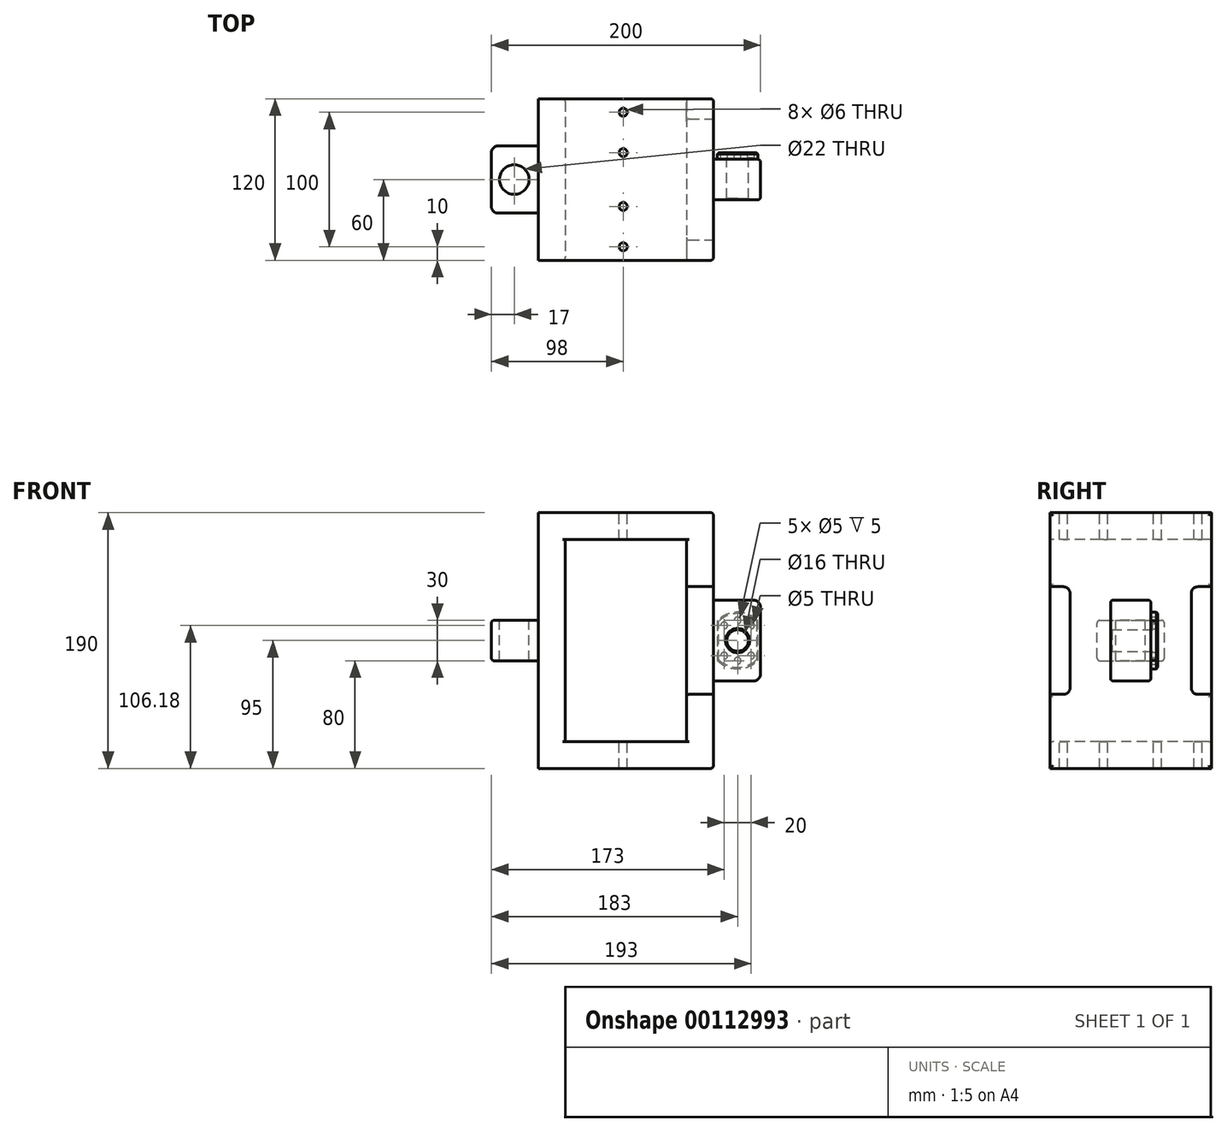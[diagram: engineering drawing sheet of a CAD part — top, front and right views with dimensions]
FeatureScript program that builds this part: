
annotation { "Feature Type Name" : "Feature", "Feature Type Description" : "" }
export const myFeature = defineFeature(function(context is Context, id is Id, definition is map)
    precondition{}
    {
        {
            var Q0;
            Q0=qCreatedBy(makeId("Front.planeOp"),FACE);
            var sketch = newSketch(context, id + "F0", { "sketchPlane" : qUnion([Q0])});
            skLineSegment(sketch, "E0.bottom", {"start": v(-45, 75) * mm, "end": v(45, 75) * mm});
            skLineSegment(sketch, "E0.top", {"start": v(-45, -75) * mm, "end": v(45, -75) * mm});
            skLineSegment(sketch, "E0.left", {"start": v(-45, 75) * mm, "end": v(-45, -75) * mm});
            skPoint(sketch, "E0.middle", {"position": v(0, 0) * mm});
            skLineSegment(sketch, "E1.bottom", {"start": v(-65, 95) * mm, "end": v(45, 95) * mm});
            skLineSegment(sketch, "E1.top", {"start": v(-65, -95) * mm, "end": v(45, -95) * mm});
            skLineSegment(sketch, "E1.left", {"start": v(-65, 95) * mm, "end": v(-65, -95) * mm});
            skLineSegment(sketch, "E2.bottom", {"start": v(45, 95) * mm, "end": v(65, 95) * mm});
            skLineSegment(sketch, "E2.top", {"start": v(45, -95) * mm, "end": v(65, -95) * mm});
            skLineSegment(sketch, "E2.left", {"start": v(45, 75) * mm, "end": v(45, -75) * mm});
            skLineSegment(sketch, "E2.right", {"start": v(65, 95) * mm, "end": v(65, -95) * mm});
            skSolve(sketch);
        }
        {
            var Q0;
            Q0=makeQuery(id+"F0.imprint","IMPRINT",FACE,{"disambiguationData":[TD([[makeQuery(id+"F0.imprint","IMPRINT",EDGE,{"derivedFrom":sQuery(id+"F0.wireOp",EDGE,"E0.bottom")}),1.0]])]});
            extrude(context, id + "F1", {"entities" : qUnion([Q0]), "oppositeDirection" : true, "depth" : 120 * mm});
        }
        {
            var Q0;
            Q0=makeQuery(id+"F1.opExtrude","SWEPT_FACE",FACE,{"disambiguationData":[OSD([sQuery(id+"F0.wireOp",EDGE,"E1.bottom")])]});
            var sketch = newSketch(context, id + "F2", { "sketchPlane" : qUnion([Q0])});
            skCircle(sketch, "E3", {"center": v(-2, 110) * mm, "radius": 3 * mm});
            skCircle(sketch, "E4", {"center": v(-2, 10) * mm, "radius": 3 * mm});
            skCircle(sketch, "E5", {"center": v(-2, 80) * mm, "radius": 3 * mm});
            skCircle(sketch, "E6", {"center": v(-2, 40) * mm, "radius": 3 * mm});
            skSolve(sketch);
        }
        {
            var Q0;
            Q0=makeQuery(id+"F2.imprint","IMPRINT",FACE,{"disambiguationData":[TD([[makeQuery(id+"F2.imprint","IMPRINT",EDGE,{"derivedFrom":sQuery(id+"F2.wireOp",EDGE,"E3")}),1.0]])]});
            var Q1;
            Q1=makeQuery(id+"F2.imprint","IMPRINT",FACE,{"disambiguationData":[TD([[makeQuery(id+"F2.imprint","IMPRINT",EDGE,{"derivedFrom":sQuery(id+"F2.wireOp",EDGE,"E5")}),1.0]])]});
            var Q2;
            Q2=makeQuery(id+"F2.imprint","IMPRINT",FACE,{"disambiguationData":[TD([[makeQuery(id+"F2.imprint","IMPRINT",EDGE,{"derivedFrom":sQuery(id+"F2.wireOp",EDGE,"E6")}),1.0]])]});
            var Q3;
            Q3=makeQuery(id+"F2.imprint","IMPRINT",FACE,{"disambiguationData":[TD([[makeQuery(id+"F2.imprint","IMPRINT",EDGE,{"derivedFrom":sQuery(id+"F2.wireOp",EDGE,"E4")}),1.0]])]});
            extrude(context, id + "F3", {"entities" : qUnion([Q0, Q1, Q2, Q3]), "operationType" : NewBodyOperationType.REMOVE, "oppositeDirection" : true, "depth" : 200 * mm});
        }
        {
            var Q0;
            Q0=makeQuery(id+"F1.opExtrude","SWEPT_FACE",FACE,{"disambiguationData":[OSD([sQuery(id+"F0.wireOp",EDGE,"E2.right")])]});
            var sketch = newSketch(context, id + "F4", { "sketchPlane" : qUnion([Q0])});
            skLineSegment(sketch, "E7.bottom", {"start": v(45, -30) * mm, "end": v(75, -30) * mm});
            skLineSegment(sketch, "E7.top", {"start": v(45, 30) * mm, "end": v(75, 30) * mm});
            skLineSegment(sketch, "E7.left", {"start": v(45, -30) * mm, "end": v(45, 30) * mm});
            skLineSegment(sketch, "E7.right", {"start": v(75, -30) * mm, "end": v(75, 30) * mm});
            skPoint(sketch, "E7.middle", {"position": v(60, 0) * mm});
            skSolve(sketch);
        }
        {
            var Q0;
            Q0=makeQuery(id+"F4.imprint","IMPRINT",FACE,{"disambiguationData":[TD([[makeQuery(id+"F4.imprint","IMPRINT",EDGE,{"derivedFrom":sQuery(id+"F4.wireOp",EDGE,"E7.bottom")}),1.0]])]});
            extrude(context, id + "F5", {"entities" : qUnion([Q0]), "operationType" : NewBodyOperationType.ADD, "depth" : 35 * mm});
        }
        {
            var Q0;
            Q0=makeQuery(id+"F5.opExtrude","SWEPT_FACE",FACE,{"disambiguationData":[OSD([sQuery(id+"F4.wireOp",EDGE,"E7.right")])]});
            var sketch = newSketch(context, id + "F6", { "sketchPlane" : qUnion([Q0])});
            skCircle(sketch, "E8", {"center": v(-83, 0) * mm, "radius": 12.5 * mm});
            skSolve(sketch);
        }
        {
            var Q0;
            Q0=makeQuery(id+"F6.imprint","IMPRINT",FACE,{"disambiguationData":[TD([[makeQuery(id+"F6.imprint","IMPRINT",EDGE,{"derivedFrom":sQuery(id+"F6.wireOp",EDGE,"E8")}),1.0]])]});
            extrude(context, id + "F7", {"entities" : qUnion([Q0]), "operationType" : NewBodyOperationType.REMOVE, "oppositeDirection" : true, "depth" : 30 * mm});
        }
        {
            var Q0;
            Q0=makeQuery(id+"F5.opExtrude","SWEPT_FACE",FACE,{"disambiguationData":[OSD([sQuery(id+"F4.wireOp",EDGE,"E7.right")])]});
            var sketch = newSketch(context, id + "F8", { "sketchPlane" : qUnion([Q0])});
            skCircle(sketch, "E9", {"center": v(-83, 0) * mm, "radius": 8 * mm});
            skCircle(sketch, "E10", {"center": v(-83, 0) * mm, "radius": 12.5 * mm});
            skSolve(sketch);
        }
        {
            var Q0;
            Q0=makeQuery(id+"F8.imprint","IMPRINT",FACE,{"disambiguationData":[TD([[makeQuery(id+"F8.imprint","IMPRINT",EDGE,{"derivedFrom":sQuery(id+"F8.wireOp",EDGE,"E9")}),-1.0]])]});
            var Q1;
            Q1=sQuery(id+"F8.wireOp",EDGE,"E9");
            var Q2;
            Q2=sQuery(id+"F8.wireOp",EDGE,"E10");
            extrude(context, id + "F9", {"entities" : qUnion([Q0]), "surfaceEntities" : qUnion([Q1, Q2]), "oppositeDirection" : true, "depth" : 30 * mm});
        }
        {
            var Q0;
            Q0=makeQuery(id+"F9.opExtrude","CAP_FACE",FACE,{"disambiguationData":[OSD([sQuery(id+"F8.wireOp",EDGE,"E9"),sQuery(id+"F8.wireOp",EDGE,"E10")])],"isStart":true});
            var sketch = newSketch(context, id + "F10", { "sketchPlane" : qUnion([Q0])});
            skArc(sketch, "E11", {"start": v(-98, -14.7) * mm, "mid": v(-83, -21) * mm, "end": v(-68, -14.7) * mm});
            skLineSegment(sketch, "E12", {"start": v(-98, 14.7) * mm, "end": v(-98, -14.7) * mm});
            skLineSegment(sketch, "E13", {"start": v(-68, 14.7) * mm, "end": v(-68, -14.7) * mm});
            skArc(sketch, "E14.trimOffspring", {"start": v(-68, 14.7) * mm, "mid": v(-83, 21) * mm, "end": v(-98, 14.7) * mm});
            skSolve(sketch);
        }
        {
            var Q0;
            Q0=makeQuery(id+"F10.imprint","IMPRINT",FACE,{"disambiguationData":[TD([[makeQuery(id+"F10.imprint","IMPRINT",EDGE,{"derivedFrom":makeQuery(id+"F9.opExtrude","CAP_EDGE",EDGE,{"disambiguationData":[OSD([sQuery(id+"F8.wireOp",EDGE,"E9")])],"isStart":true})}),1.0]])]});
            var Q1;
            Q1=makeQuery(id+"F10.imprint","IMPRINT",FACE,{"disambiguationData":[TD([[makeQuery(id+"F10.imprint","IMPRINT",EDGE,{"derivedFrom":makeQuery(id+"F9.opExtrude","CAP_EDGE",EDGE,{"disambiguationData":[OSD([sQuery(id+"F8.wireOp",EDGE,"E9")])],"isStart":true})}),-1.0]])]});
            var Q2;
            Q2=makeQuery(id+"F10.imprint","IMPRINT",FACE,{"disambiguationData":[TD([[makeQuery(id+"F10.imprint","IMPRINT",EDGE,{"derivedFrom":sQuery(id+"F10.wireOp",EDGE,"E11")}),1.0]])]});
            extrude(context, id + "F11", {"entities" : qUnion([Q0, Q1, Q2]), "operationType" : NewBodyOperationType.ADD, "depth" : 5 * mm});
        }
        {
            var Q0;
            Q0=makeQuery(id+"F11.opExtrude","CAP_FACE",FACE,{"disambiguationData":[OSD([sQuery(id+"F10.wireOp",EDGE,"E11")])],"isStart":false});
            var sketch = newSketch(context, id + "F12", { "sketchPlane" : qUnion([Q0])});
            skCircle(sketch, "E15", {"center": v(-83, 0) * mm, "radius": 8 * mm});
            skSolve(sketch);
        }
        {
            var Q0;
            Q0=makeQuery(id+"F12.imprint","IMPRINT",FACE,{"disambiguationData":[TD([[makeQuery(id+"F12.imprint","IMPRINT",EDGE,{"derivedFrom":sQuery(id+"F12.wireOp",EDGE,"E15")}),1.0]])]});
            extrude(context, id + "F13", {"entities" : qUnion([Q0]), "operationType" : NewBodyOperationType.REMOVE, "oppositeDirection" : true, "depth" : 25 * mm});
        }
        {
            var Q0;
            Q0=makeQuery(id+"F11.opExtrude","CAP_EDGE",EDGE,{"disambiguationData":[OSD([sQuery(id+"F10.wireOp",EDGE,"E11")])],"isStart":false});
            var Q1;
            Q1=makeQuery(id+"F13.boolean.opBoolean","COPY",EDGE,{"derivedFrom":makeQuery(id+"F13.opExtrude","CAP_EDGE",EDGE,{"disambiguationData":[OSD([sQuery(id+"F12.wireOp",EDGE,"E15")])],"isStart":true})});
            var Q2;
            Q2=makeQuery(id+"F9.opExtrude","CAP_EDGE",EDGE,{"disambiguationData":[OSD([sQuery(id+"F8.wireOp",EDGE,"E9")])],"isStart":false});
            var Q3;
            Q3=makeQuery(id+"F11.opExtrude","CAP_EDGE",EDGE,{"disambiguationData":[OSD([sQuery(id+"F10.wireOp",EDGE,"E14.trimOffspring")])],"isStart":false});
            var Q4;
            Q4=makeQuery(id+"F11.opExtrude","CAP_EDGE",EDGE,{"disambiguationData":[OSD([sQuery(id+"F10.wireOp",EDGE,"E12")])],"isStart":false});
            var Q5;
            Q5=makeQuery(id+"F11.opExtrude","CAP_EDGE",EDGE,{"disambiguationData":[OSD([sQuery(id+"F10.wireOp",EDGE,"E13")])],"isStart":false});
            chamfer(context, id + "F14", {"entities" : qUnion([Q0, Q1, Q2, Q3, Q4, Q5]), "width" : 1 * mm, "tangentPropagation" : true});
        }
        {
            var Q0;
            Q0=makeQuery(id+"F1.opExtrude","SWEPT_FACE",FACE,{"disambiguationData":[OSD([sQuery(id+"F0.wireOp",EDGE,"E2.right")])]});
            var sketch = newSketch(context, id + "F15", { "sketchPlane" : qUnion([Q0])});
            skLineSegment(sketch, "E16.bottom", {"start": v(0, -40) * mm, "end": v(10, -40) * mm});
            skLineSegment(sketch, "E16.top", {"start": v(0, 40) * mm, "end": v(10, 40) * mm});
            skLineSegment(sketch, "E16.left", {"start": v(0, -40) * mm, "end": v(0, 40) * mm});
            skLineSegment(sketch, "E16.right", {"start": v(15, -35) * mm, "end": v(15, 35) * mm});
            skPoint(sketch, "E16.middle", {"position": v(7.5, 0) * mm});
            skLineSegment(sketch, "E17.bottom", {"start": v(120, -40) * mm, "end": v(110, -40) * mm});
            skLineSegment(sketch, "E17.top", {"start": v(120, 40) * mm, "end": v(110, 40) * mm});
            skLineSegment(sketch, "E17.left", {"start": v(120, -40) * mm, "end": v(120, 40) * mm});
            skLineSegment(sketch, "E17.right", {"start": v(105, -35) * mm, "end": v(105, 35) * mm});
            skPoint(sketch, "E17.middle", {"position": v(112.5, 0) * mm});
            skPoint(sketch, "E18.visualSharp", {"position": v(105, 40) * mm});
            skArc(sketch, "E18.filletArc", {"start": v(110, 40) * mm, "mid": v(106.46, 38.54) * mm, "end": v(105, 35) * mm});
            skPoint(sketch, "E19.visualSharp", {"position": v(105, -40) * mm});
            skArc(sketch, "E19.filletArc", {"start": v(105, -35) * mm, "mid": v(106.46, -38.54) * mm, "end": v(110, -40) * mm});
            skPoint(sketch, "E20.visualSharp", {"position": v(15, -40) * mm});
            skArc(sketch, "E20.filletArc", {"start": v(10, -40) * mm, "mid": v(13.54, -38.54) * mm, "end": v(15, -35) * mm});
            skPoint(sketch, "E21.visualSharp", {"position": v(15, 40) * mm});
            skArc(sketch, "E21.filletArc", {"start": v(15, 35) * mm, "mid": v(13.54, 38.54) * mm, "end": v(10, 40) * mm});
            skSolve(sketch);
        }
        {
            var Q0;
            Q0=makeQuery(id+"F15.imprint","IMPRINT",FACE,{"disambiguationData":[TD([[makeQuery(id+"F15.imprint","IMPRINT",EDGE,{"derivedFrom":sQuery(id+"F15.wireOp",EDGE,"E16.bottom")}),1.0]])]});
            var Q1;
            Q1=makeQuery(id+"F15.imprint","IMPRINT",FACE,{"disambiguationData":[TD([[makeQuery(id+"F15.imprint","IMPRINT",EDGE,{"derivedFrom":sQuery(id+"F15.wireOp",EDGE,"E17.bottom")}),-1.0]])]});
            extrude(context, id + "F16", {"entities" : qUnion([Q0, Q1]), "operationType" : NewBodyOperationType.REMOVE, "oppositeDirection" : true, "depth" : 25 * mm});
        }
        {
            var Q0;
            Q0=makeQuery(id+"F1.opExtrude","SWEPT_FACE",FACE,{"disambiguationData":[OSD([sQuery(id+"F0.wireOp",EDGE,"E1.left")])]});
            var sketch = newSketch(context, id + "F17", { "sketchPlane" : qUnion([Q0])});
            skLineSegment(sketch, "E22.bottom", {"start": v(-35, -15) * mm, "end": v(-85, -15) * mm});
            skLineSegment(sketch, "E22.top", {"start": v(-35, 15) * mm, "end": v(-85, 15) * mm});
            skLineSegment(sketch, "E22.left", {"start": v(-35, -15) * mm, "end": v(-35, 15) * mm});
            skLineSegment(sketch, "E22.right", {"start": v(-85, -15) * mm, "end": v(-85, 15) * mm});
            skPoint(sketch, "E22.middle", {"position": v(-60, 0) * mm});
            skSolve(sketch);
        }
        {
            var Q0;
            Q0=makeQuery(id+"F17.imprint","IMPRINT",FACE,{"disambiguationData":[TD([[makeQuery(id+"F17.imprint","IMPRINT",EDGE,{"derivedFrom":sQuery(id+"F17.wireOp",EDGE,"E22.bottom")}),-1.0]])]});
            extrude(context, id + "F18", {"entities" : qUnion([Q0]), "operationType" : NewBodyOperationType.ADD, "depth" : 35 * mm});
        }
        {
            var Q0;
            Q0=makeQuery(id+"F18.opExtrude","SWEPT_FACE",FACE,{"disambiguationData":[OSD([sQuery(id+"F17.wireOp",EDGE,"E22.top")])]});
            var sketch = newSketch(context, id + "F19", { "sketchPlane" : qUnion([Q0])});
            skCircle(sketch, "E23", {"center": v(-83, 60) * mm, "radius": 11 * mm});
            skSolve(sketch);
        }
        {
            var Q0;
            Q0=makeQuery(id+"F19.imprint","IMPRINT",FACE,{"disambiguationData":[TD([[makeQuery(id+"F19.imprint","IMPRINT",EDGE,{"derivedFrom":sQuery(id+"F19.wireOp",EDGE,"E23")}),1.0]])]});
            extrude(context, id + "F20", {"entities" : qUnion([Q0]), "operationType" : NewBodyOperationType.REMOVE, "oppositeDirection" : true, "depth" : 30 * mm});
        }
        {
            var Q0;
            Q0=makeQuery(id+"F18.opExtrude","CAP_EDGE",EDGE,{"disambiguationData":[OSD([sQuery(id+"F17.wireOp",EDGE,"E22.left")])],"isStart":false});
            var Q1;
            Q1=makeQuery(id+"F18.opExtrude","CAP_EDGE",EDGE,{"disambiguationData":[OSD([sQuery(id+"F17.wireOp",EDGE,"E22.right")])],"isStart":false});
            fillet(context, id + "F21", {"entities" : qUnion([Q0, Q1]), "radius" : 5 * mm, "tangentPropagation" : true, "allowEdgeOverflow" : false});
        }
        {
            var Q0;
            Q0=makeQuery(id+"F11.opExtrude","CAP_FACE",FACE,{"disambiguationData":[OSD([sQuery(id+"F10.wireOp",EDGE,"E11"),sQuery(id+"F10.wireOp",EDGE,"E12"),sQuery(id+"F10.wireOp",EDGE,"E13"),sQuery(id+"F10.wireOp",EDGE,"E14.trimOffspring")])],"isStart":false});
            var sketch = newSketch(context, id + "F22", { "sketchPlane" : qUnion([Q0])});
            skCircle(sketch, "E24", {"center": v(-83, 0) * mm, "radius": 15 * mm, "construction": true});
            skCircle(sketch, "E25", {"center": v(-83, 15) * mm, "radius": 2.5 * mm});
            skCircle(sketch, "E26", {"center": v(-83, -15) * mm, "radius": 2.5 * mm});
            skCircle(sketch, "E27", {"center": v(-93, 11.18) * mm, "radius": 2.5 * mm});
            skCircle(sketch, "E28", {"center": v(-73, 11.18) * mm, "radius": 2.5 * mm});
            skCircle(sketch, "E29", {"center": v(-93, -11.18) * mm, "radius": 2.5 * mm});
            skCircle(sketch, "E30", {"center": v(-73, -11.18) * mm, "radius": 2.5 * mm});
            skSolve(sketch);
        }
        {
            var Q0;
            Q0=makeQuery(id+"F22.imprint","IMPRINT",FACE,{"disambiguationData":[TD([[makeQuery(id+"F22.imprint","IMPRINT",EDGE,{"derivedFrom":sQuery(id+"F22.wireOp",EDGE,"E27")}),1.0]])]});
            var Q1;
            Q1=makeQuery(id+"F22.imprint","IMPRINT",FACE,{"disambiguationData":[TD([[makeQuery(id+"F22.imprint","IMPRINT",EDGE,{"derivedFrom":sQuery(id+"F22.wireOp",EDGE,"E25")}),1.0]])]});
            var Q2;
            Q2=makeQuery(id+"F22.imprint","IMPRINT",FACE,{"disambiguationData":[TD([[makeQuery(id+"F22.imprint","IMPRINT",EDGE,{"derivedFrom":sQuery(id+"F22.wireOp",EDGE,"E28")}),1.0]])]});
            var Q3;
            Q3=makeQuery(id+"F22.imprint","IMPRINT",FACE,{"disambiguationData":[TD([[makeQuery(id+"F22.imprint","IMPRINT",EDGE,{"derivedFrom":sQuery(id+"F22.wireOp",EDGE,"E30")}),1.0]])]});
            var Q4;
            Q4=makeQuery(id+"F22.imprint","IMPRINT",FACE,{"disambiguationData":[TD([[makeQuery(id+"F22.imprint","IMPRINT",EDGE,{"derivedFrom":sQuery(id+"F22.wireOp",EDGE,"E26")}),1.0]])]});
            var Q5;
            Q5=makeQuery(id+"F22.imprint","IMPRINT",FACE,{"disambiguationData":[TD([[makeQuery(id+"F22.imprint","IMPRINT",EDGE,{"derivedFrom":sQuery(id+"F22.wireOp",EDGE,"E29")}),1.0]])]});
            extrude(context, id + "F23", {"entities" : qUnion([Q0, Q1, Q2, Q3, Q4, Q5]), "operationType" : NewBodyOperationType.REMOVE, "oppositeDirection" : true, "depth" : 5 * mm});
        }
        {
            var Q0;
            Q0=makeQuery(id+"F23.boolean.opBoolean","COPY",EDGE,{"derivedFrom":makeQuery(id+"F23.opExtrude","CAP_EDGE",EDGE,{"disambiguationData":[OSD([sQuery(id+"F22.wireOp",EDGE,"E27")])],"isStart":false})});
            var Q1;
            Q1=makeQuery(id+"F23.boolean.opBoolean","COPY",EDGE,{"derivedFrom":makeQuery(id+"F23.opExtrude","CAP_EDGE",EDGE,{"disambiguationData":[OSD([sQuery(id+"F22.wireOp",EDGE,"E25")])],"isStart":true})});
            var Q2;
            Q2=makeQuery(id+"F23.boolean.opBoolean","COPY",EDGE,{"derivedFrom":makeQuery(id+"F23.opExtrude","CAP_EDGE",EDGE,{"disambiguationData":[OSD([sQuery(id+"F22.wireOp",EDGE,"E28")])],"isStart":true})});
            var Q3;
            Q3=makeQuery(id+"F23.boolean.opBoolean","COPY",EDGE,{"derivedFrom":makeQuery(id+"F23.opExtrude","CAP_EDGE",EDGE,{"disambiguationData":[OSD([sQuery(id+"F22.wireOp",EDGE,"E30")])],"isStart":true})});
            var Q4;
            Q4=makeQuery(id+"F23.boolean.opBoolean","COPY",EDGE,{"derivedFrom":makeQuery(id+"F23.opExtrude","CAP_EDGE",EDGE,{"disambiguationData":[OSD([sQuery(id+"F22.wireOp",EDGE,"E26")])],"isStart":true})});
            var Q5;
            Q5=makeQuery(id+"F23.boolean.opBoolean","COPY",EDGE,{"derivedFrom":makeQuery(id+"F23.opExtrude","CAP_EDGE",EDGE,{"disambiguationData":[OSD([sQuery(id+"F22.wireOp",EDGE,"E29")])],"isStart":true})});
            var Q6;
            Q6=makeQuery(id+"F23.boolean.opBoolean","COPY",EDGE,{"derivedFrom":makeQuery(id+"F23.opExtrude","CAP_EDGE",EDGE,{"disambiguationData":[OSD([sQuery(id+"F22.wireOp",EDGE,"E27")])],"isStart":true})});
            chamfer(context, id + "F24", {"entities" : qUnion([Q0, Q1, Q2, Q3, Q4, Q5, Q6]), "width" : 1 * mm, "tangentPropagation" : true});
        }
        {
            var Q0;
            Q0=makeQuery(id+"F5.opExtrude","CAP_EDGE",EDGE,{"disambiguationData":[OSD([sQuery(id+"F4.wireOp",EDGE,"E7.top")])],"isStart":false});
            var Q1;
            Q1=makeQuery(id+"F5.opExtrude","CAP_EDGE",EDGE,{"disambiguationData":[OSD([sQuery(id+"F4.wireOp",EDGE,"E7.bottom")])],"isStart":false});
            fillet(context, id + "F25", {"entities" : qUnion([Q0, Q1]), "radius" : 5 * mm, "tangentPropagation" : true, "allowEdgeOverflow" : false});
        }
        {
            var Q0;
            Q0=makeQuery(id+"F5.opExtrude","CAP_EDGE",EDGE,{"disambiguationData":[OSD([sQuery(id+"F4.wireOp",EDGE,"E7.left")])],"isStart":false});
            var Q1;
            Q1=makeQuery(id+"F5.opExtrude","CAP_EDGE",EDGE,{"disambiguationData":[OSD([sQuery(id+"F4.wireOp",EDGE,"E7.right")])],"isStart":false});
            var Q2;
            Q2=makeQuery(id+"F18.opExtrude","CAP_EDGE",EDGE,{"disambiguationData":[OSD([sQuery(id+"F17.wireOp",EDGE,"E22.top")])],"isStart":false});
            var Q3;
            Q3=makeQuery(id+"F18.opExtrude","CAP_EDGE",EDGE,{"disambiguationData":[OSD([sQuery(id+"F17.wireOp",EDGE,"E22.bottom")])],"isStart":false});
            fillet(context, id + "F26", {"entities" : qUnion([Q0, Q1, Q2, Q3]), "radius" : 2 * mm, "tangentPropagation" : true, "allowEdgeOverflow" : false});
        }
        {
            var Q0;
            {var subQ0=sQuery(id+"F0.wireOp",EDGE,"E2.right");Q0=makeQuery(id+"F16.boolean.opBoolean","SPLIT",EDGE,{"disambiguationData":[TD([makeQuery(id+"F16.opExtrude","SWEPT_FACE",FACE,{"disambiguationData":[OSD([sQuery(id+"F15.wireOp",EDGE,"E17.top")])]})])],"derivedFrom":makeQuery(id+"F1.opExtrude","CAP_EDGE",EDGE,{"disambiguationData":[OSD([subQ0])],"isStart":false})});}
            var Q1;
            Q1=makeQuery(id+"F1.opExtrude","SWEPT_EDGE",EDGE,{"disambiguationData":[OSD([sQuery(id+"F0.wireOp",EDGE,"E2.bottom"),sQuery(id+"F0.wireOp",EDGE,"E2.right")])]});
            var Q2;
            {var subQ0=sQuery(id+"F0.wireOp",EDGE,"E2.right");Q2=makeQuery(id+"F16.boolean.opBoolean","SPLIT",EDGE,{"disambiguationData":[TD([makeQuery(id+"F16.opExtrude","SWEPT_FACE",FACE,{"disambiguationData":[OSD([sQuery(id+"F15.wireOp",EDGE,"E16.top")])]})])],"derivedFrom":makeQuery(id+"F1.opExtrude","CAP_EDGE",EDGE,{"disambiguationData":[OSD([subQ0])],"isStart":true})});}
            var Q3;
            Q3=makeQuery(id+"F16.boolean.opBoolean","COPY",EDGE,{"derivedFrom":makeQuery(id+"F16.opExtrude","CAP_EDGE",EDGE,{"disambiguationData":[OSD([sQuery(id+"F15.wireOp",EDGE,"E16.top")])],"isStart":true})});
            var Q4;
            Q4=makeQuery(id+"F16.boolean.opBoolean","COPY",EDGE,{"derivedFrom":makeQuery(id+"F16.opExtrude","CAP_EDGE",EDGE,{"disambiguationData":[OSD([sQuery(id+"F15.wireOp",EDGE,"E21.filletArc")])],"isStart":true})});
            var Q5;
            Q5=makeQuery(id+"F16.boolean.opBoolean","COPY",EDGE,{"derivedFrom":makeQuery(id+"F16.opExtrude","CAP_EDGE",EDGE,{"disambiguationData":[OSD([sQuery(id+"F15.wireOp",EDGE,"E16.right")])],"isStart":true})});
            var Q6;
            Q6=makeQuery(id+"F16.boolean.opBoolean","COPY",EDGE,{"derivedFrom":makeQuery(id+"F16.opExtrude","CAP_EDGE",EDGE,{"disambiguationData":[OSD([sQuery(id+"F15.wireOp",EDGE,"E20.filletArc")])],"isStart":true})});
            var Q7;
            Q7=makeQuery(id+"F16.boolean.opBoolean","COPY",EDGE,{"derivedFrom":makeQuery(id+"F16.opExtrude","CAP_EDGE",EDGE,{"disambiguationData":[OSD([sQuery(id+"F15.wireOp",EDGE,"E16.bottom")])],"isStart":true})});
            var Q8;
            {var subQ0=sQuery(id+"F0.wireOp",EDGE,"E2.right");Q8=makeQuery(id+"F16.boolean.opBoolean","SPLIT",EDGE,{"disambiguationData":[TD([makeQuery(id+"F16.opExtrude","SWEPT_FACE",FACE,{"disambiguationData":[OSD([sQuery(id+"F15.wireOp",EDGE,"E16.bottom")])]})])],"derivedFrom":makeQuery(id+"F1.opExtrude","CAP_EDGE",EDGE,{"disambiguationData":[OSD([subQ0])],"isStart":true})});}
            var Q9;
            Q9=makeQuery(id+"F1.opExtrude","SWEPT_EDGE",EDGE,{"disambiguationData":[OSD([sQuery(id+"F0.wireOp",EDGE,"E2.top"),sQuery(id+"F0.wireOp",EDGE,"E2.right")])]});
            var Q10;
            {var subQ0=sQuery(id+"F0.wireOp",EDGE,"E2.right");Q10=makeQuery(id+"F16.boolean.opBoolean","SPLIT",EDGE,{"disambiguationData":[TD([makeQuery(id+"F16.opExtrude","SWEPT_FACE",FACE,{"disambiguationData":[OSD([sQuery(id+"F15.wireOp",EDGE,"E17.bottom")])]})])],"derivedFrom":makeQuery(id+"F1.opExtrude","CAP_EDGE",EDGE,{"disambiguationData":[OSD([subQ0])],"isStart":false})});}
            var Q11;
            Q11=makeQuery(id+"F16.boolean.opBoolean","COPY",EDGE,{"derivedFrom":makeQuery(id+"F16.opExtrude","CAP_EDGE",EDGE,{"disambiguationData":[OSD([sQuery(id+"F15.wireOp",EDGE,"E17.bottom")])],"isStart":true})});
            var Q12;
            Q12=makeQuery(id+"F16.boolean.opBoolean","COPY",EDGE,{"derivedFrom":makeQuery(id+"F16.opExtrude","CAP_EDGE",EDGE,{"disambiguationData":[OSD([sQuery(id+"F15.wireOp",EDGE,"E19.filletArc")])],"isStart":true})});
            var Q13;
            Q13=makeQuery(id+"F16.boolean.opBoolean","COPY",EDGE,{"derivedFrom":makeQuery(id+"F16.opExtrude","CAP_EDGE",EDGE,{"disambiguationData":[OSD([sQuery(id+"F15.wireOp",EDGE,"E17.right")])],"isStart":true})});
            var Q14;
            Q14=makeQuery(id+"F16.boolean.opBoolean","COPY",EDGE,{"derivedFrom":makeQuery(id+"F16.opExtrude","CAP_EDGE",EDGE,{"disambiguationData":[OSD([sQuery(id+"F15.wireOp",EDGE,"E18.filletArc")])],"isStart":true})});
            var Q15;
            Q15=makeQuery(id+"F16.boolean.opBoolean","COPY",EDGE,{"derivedFrom":makeQuery(id+"F16.opExtrude","CAP_EDGE",EDGE,{"disambiguationData":[OSD([sQuery(id+"F15.wireOp",EDGE,"E17.top")])],"isStart":true})});
            var Q16;
            Q16=makeQuery(id+"F16.boolean.opBoolean","COPY",EDGE,{"derivedFrom":makeQuery(id+"F16.opExtrude","SWEPT_EDGE",EDGE,{"disambiguationData":[OSD([sQuery(id+"F0.wireOp",EDGE,"E2.right"),sQuery(id+"F15.wireOp",EDGE,"E16.bottom"),sQuery(id+"F15.wireOp",EDGE,"E16.left")])]})});
            var Q17;
            Q17=makeQuery(id+"F16.boolean.opBoolean","COPY",EDGE,{"derivedFrom":makeQuery(id+"F16.opExtrude","SWEPT_EDGE",EDGE,{"disambiguationData":[OSD([sQuery(id+"F0.wireOp",EDGE,"E2.right"),sQuery(id+"F15.wireOp",EDGE,"E16.top"),sQuery(id+"F15.wireOp",EDGE,"E16.left")])]})});
            var Q18;
            Q18=makeQuery(id+"F16.boolean.opBoolean","COPY",EDGE,{"derivedFrom":makeQuery(id+"F16.opExtrude","SWEPT_EDGE",EDGE,{"disambiguationData":[OSD([sQuery(id+"F0.wireOp",EDGE,"E2.right"),sQuery(id+"F15.wireOp",EDGE,"E17.top"),sQuery(id+"F15.wireOp",EDGE,"E17.left")])]})});
            var Q19;
            Q19=makeQuery(id+"F16.boolean.opBoolean","COPY",EDGE,{"derivedFrom":makeQuery(id+"F16.opExtrude","SWEPT_EDGE",EDGE,{"disambiguationData":[OSD([sQuery(id+"F0.wireOp",EDGE,"E2.right"),sQuery(id+"F15.wireOp",EDGE,"E17.bottom"),sQuery(id+"F15.wireOp",EDGE,"E17.left")])]})});
            var Q20;
            {var subQ0=sQuery(id+"F0.wireOp",EDGE,"E0.bottom");var subQ1=sQuery(id+"F0.wireOp",EDGE,"E2.left");Q20=makeQuery(id+"F16.boolean.opBoolean","SPLIT",EDGE,{"disambiguationData":[TD([makeQuery(id+"F1.opExtrude","SWEPT_FACE",FACE,{"disambiguationData":[OSD([subQ0])]})])],"derivedFrom":makeQuery(id+"F1.opExtrude","CAP_EDGE",EDGE,{"disambiguationData":[OSD([subQ1])],"isStart":false})});}
            var Q21;
            Q21=makeQuery(id+"F16.boolean.opBoolean","INTERSECT",EDGE,{"derivedFrom":[makeQuery(id+"F1.opExtrude","SWEPT_FACE",FACE,{"disambiguationData":[OSD([sQuery(id+"F0.wireOp",EDGE,"E2.left")])]}),makeQuery(id+"F16.opExtrude","SWEPT_FACE",FACE,{"disambiguationData":[OSD([sQuery(id+"F15.wireOp",EDGE,"E17.right")])]})]});
            var Q22;
            Q22=makeQuery(id+"F16.boolean.opBoolean","INTERSECT",EDGE,{"derivedFrom":[makeQuery(id+"F1.opExtrude","SWEPT_FACE",FACE,{"disambiguationData":[OSD([sQuery(id+"F0.wireOp",EDGE,"E2.left")])]}),makeQuery(id+"F16.opExtrude","SWEPT_FACE",FACE,{"disambiguationData":[OSD([sQuery(id+"F15.wireOp",EDGE,"E18.filletArc")])]})]});
            var Q23;
            {var subQ0=sQuery(id+"F0.wireOp",EDGE,"E2.left");var subQ1=sQuery(id+"F0.wireOp",EDGE,"E0.top");Q23=makeQuery(id+"F16.boolean.opBoolean","SPLIT",EDGE,{"disambiguationData":[TD([makeQuery(id+"F1.opExtrude","SWEPT_FACE",FACE,{"disambiguationData":[OSD([subQ1])]})])],"derivedFrom":makeQuery(id+"F1.opExtrude","CAP_EDGE",EDGE,{"disambiguationData":[OSD([subQ0])],"isStart":false})});}
            var Q24;
            Q24=makeQuery(id+"F1.opExtrude","CAP_EDGE",EDGE,{"disambiguationData":[OSD([sQuery(id+"F0.wireOp",EDGE,"E0.left")])],"isStart":false});
            var Q25;
            Q25=makeQuery(id+"F1.opExtrude","CAP_EDGE",EDGE,{"disambiguationData":[OSD([sQuery(id+"F0.wireOp",EDGE,"E0.left")])],"isStart":true});
            var Q26;
            Q26=makeQuery(id+"F16.boolean.opBoolean","INTERSECT",EDGE,{"derivedFrom":[makeQuery(id+"F1.opExtrude","SWEPT_FACE",FACE,{"disambiguationData":[OSD([sQuery(id+"F0.wireOp",EDGE,"E2.left")])]}),makeQuery(id+"F16.opExtrude","SWEPT_FACE",FACE,{"disambiguationData":[OSD([sQuery(id+"F15.wireOp",EDGE,"E16.right")])]})]});
            var Q27;
            {var subQ0=sQuery(id+"F0.wireOp",EDGE,"E2.left");var subQ1=sQuery(id+"F0.wireOp",EDGE,"E0.top");Q27=makeQuery(id+"F16.boolean.opBoolean","SPLIT",EDGE,{"disambiguationData":[TD([makeQuery(id+"F1.opExtrude","SWEPT_FACE",FACE,{"disambiguationData":[OSD([subQ1])]})])],"derivedFrom":makeQuery(id+"F1.opExtrude","CAP_EDGE",EDGE,{"disambiguationData":[OSD([subQ0])],"isStart":true})});}
            var Q28;
            {var subQ0=sQuery(id+"F0.wireOp",EDGE,"E0.bottom");var subQ1=sQuery(id+"F0.wireOp",EDGE,"E2.left");Q28=makeQuery(id+"F16.boolean.opBoolean","SPLIT",EDGE,{"disambiguationData":[TD([makeQuery(id+"F1.opExtrude","SWEPT_FACE",FACE,{"disambiguationData":[OSD([subQ0])]})])],"derivedFrom":makeQuery(id+"F1.opExtrude","CAP_EDGE",EDGE,{"disambiguationData":[OSD([subQ1])],"isStart":true})});}
            fillet(context, id + "F27", {"entities" : qUnion([Q0, Q1, Q2, Q3, Q4, Q5, Q6, Q7, Q8, Q9, Q10, Q11, Q12, Q13, Q14, Q15, Q16, Q17, Q18, Q19, Q20, Q21, Q22, Q23, Q24, Q25, Q26, Q27, Q28]), "radius" : 2 * mm, "tangentPropagation" : true, "allowEdgeOverflow" : false});
        }
    });
